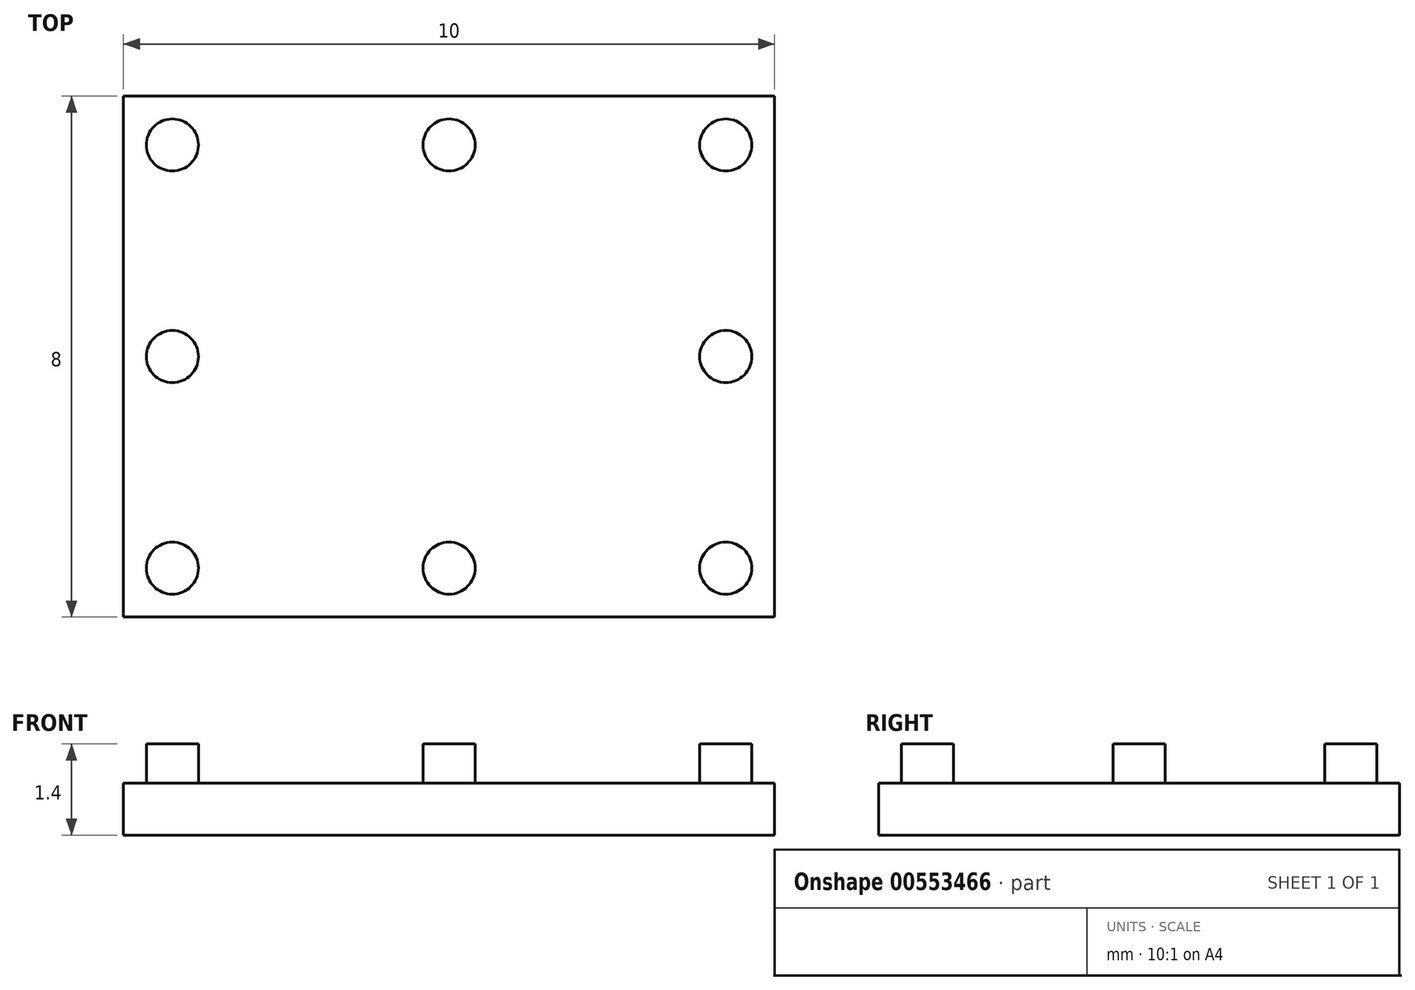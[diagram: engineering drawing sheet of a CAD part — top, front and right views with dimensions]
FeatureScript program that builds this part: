
annotation { "Feature Type Name" : "Feature", "Feature Type Description" : "" }
export const myFeature = defineFeature(function(context is Context, id is Id, definition is map)
    precondition{}
    {
        {
            var Q0;
            Q0=qCreatedBy(makeId("Top.planeOp"),FACE);
            var sketch = newSketch(context, id + "F0", { "sketchPlane" : qUnion([Q0])});
            skLineSegment(sketch, "E0.bottom", {"start": v(-5, -4) * mm, "end": v(5, -4) * mm});
            skLineSegment(sketch, "E0.top", {"start": v(-5, 4) * mm, "end": v(5, 4) * mm});
            skLineSegment(sketch, "E0.left", {"start": v(-5, -4) * mm, "end": v(-5, 4) * mm});
            skLineSegment(sketch, "E0.right", {"start": v(5, -4) * mm, "end": v(5, 4) * mm});
            skPoint(sketch, "E0.middle", {"position": v(0, 0) * mm});
            skSolve(sketch);
        }
        {
            var Q0;
            Q0=qSketchRegion(id+"F0",true);
            extrude(context, id + "F1", {"entities" : qUnion([Q0]), "depth" : 0.8 * mm, "offsetDistance" : 25 * mm});
        }
        {
            var Q0;
            Q0=makeQuery(id+"F1.opExtrude","CAP_FACE",FACE,{"disambiguationData":[OSD([sQuery(id+"F0.wireOp",EDGE,"E0.bottom"),sQuery(id+"F0.wireOp",EDGE,"E0.top"),sQuery(id+"F0.wireOp",EDGE,"E0.left"),sQuery(id+"F0.wireOp",EDGE,"E0.right")])],"isStart":false});
            var sketch = newSketch(context, id + "F2", { "sketchPlane" : qUnion([Q0])});
            skLineSegment(sketch, "E1.bottom", {"start": v(-4.25, 3.25) * mm, "end": v(4.25, 3.25) * mm, "construction": true});
            skLineSegment(sketch, "E1.top", {"start": v(-4.25, -3.25) * mm, "end": v(4.25, -3.25) * mm, "construction": true});
            skLineSegment(sketch, "E1.left", {"start": v(-4.25, 3.25) * mm, "end": v(-4.25, -3.25) * mm, "construction": true});
            skLineSegment(sketch, "E1.right", {"start": v(4.25, 3.25) * mm, "end": v(4.25, -3.25) * mm, "construction": true});
            skPoint(sketch, "E1.middle", {"position": v(0, 0) * mm});
            skCircle(sketch, "E2", {"center": v(-4.25, 3.25) * mm, "radius": 0.4 * mm});
            skCircle(sketch, "E3", {"center": v(-4.25, 0) * mm, "radius": 0.4 * mm});
            skCircle(sketch, "E4", {"center": v(-4.25, -3.25) * mm, "radius": 0.4 * mm});
            skCircle(sketch, "E5", {"center": v(0, 3.25) * mm, "radius": 0.4 * mm});
            skCircle(sketch, "E6", {"center": v(4.25, 3.25) * mm, "radius": 0.4 * mm});
            skCircle(sketch, "E7", {"center": v(4.25, 0) * mm, "radius": 0.4 * mm});
            skCircle(sketch, "E8", {"center": v(4.25, -3.25) * mm, "radius": 0.4 * mm});
            skCircle(sketch, "E9", {"center": v(0, -3.25) * mm, "radius": 0.4 * mm});
            skSolve(sketch);
        }
        {
            var Q0;
            Q0=qSketchRegion(id+"F2",true);
            extrude(context, id + "F3", {"entities" : qUnion([Q0]), "operationType" : NewBodyOperationType.ADD, "depth" : 0.6 * mm, "offsetDistance" : 25 * mm});
        }
    });
